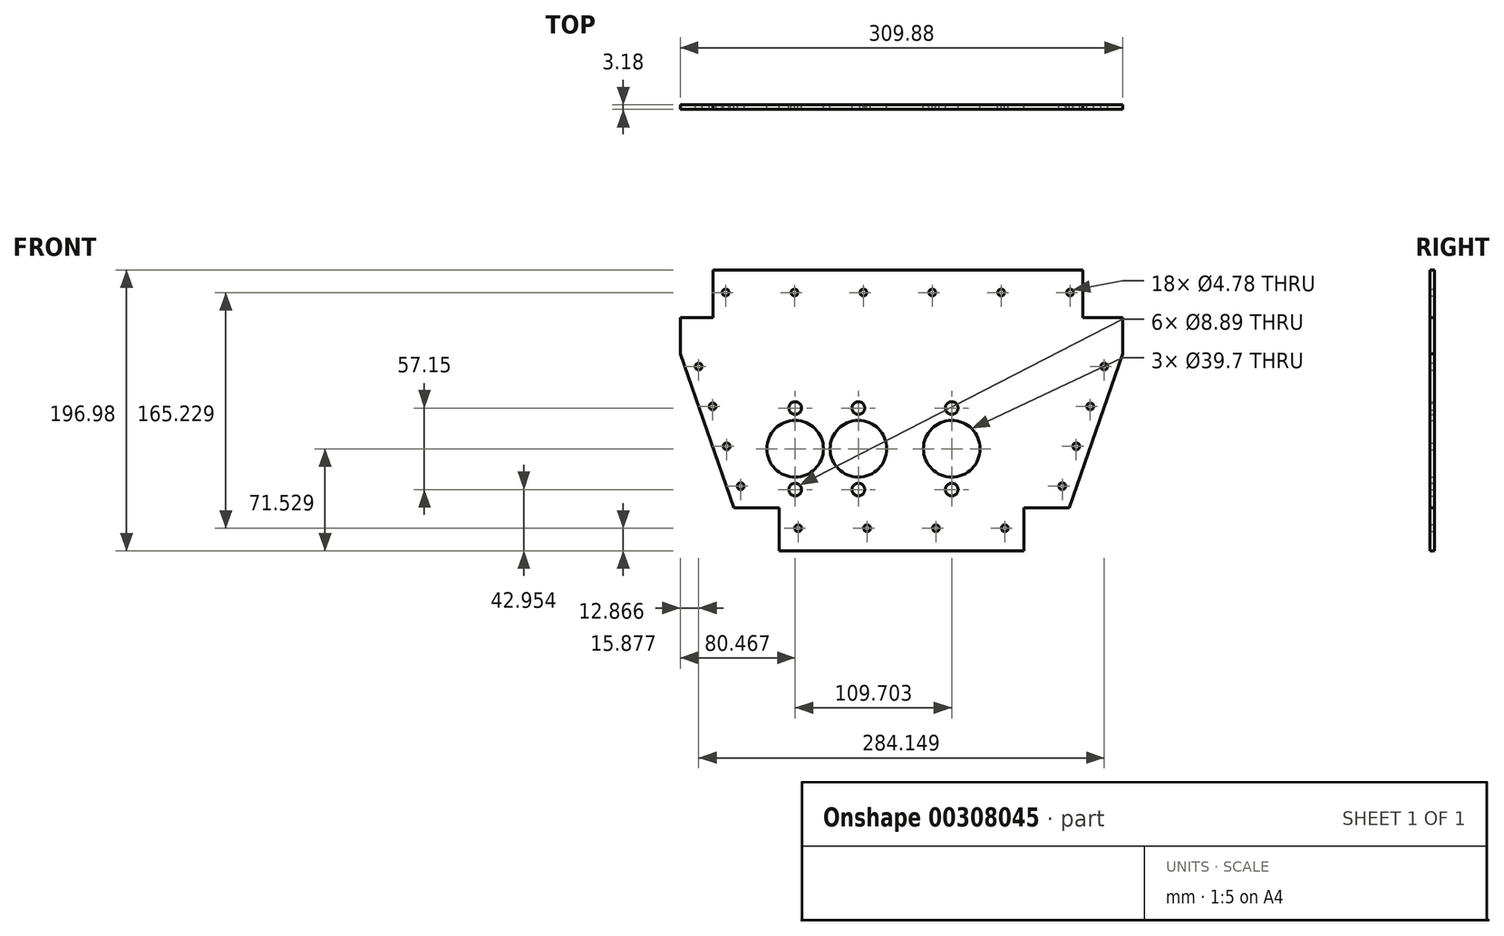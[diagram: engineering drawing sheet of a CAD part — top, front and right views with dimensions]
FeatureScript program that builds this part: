
annotation { "Feature Type Name" : "Feature", "Feature Type Description" : "" }
export const myFeature = defineFeature(function(context is Context, id is Id, definition is map)
    precondition{}
    {
        {
            var Q0;
            Q0=qCreatedBy(makeId("Front.planeOp"),FACE);
            var sketch = newSketch(context, id + "F0", { "sketchPlane" : qUnion([Q0])});
            skLineSegment(sketch, "E0.bottom", {"start": v(85.73, -97.64) * mm, "end": v(-85.73, -97.64) * mm});
            skLineSegment(sketch, "E0.top", {"start": v(127, 99.34) * mm, "end": v(-132.08, 99.34) * mm});
            skPoint(sketch, "E0.middle", {"position": v(0, 0) * mm});
            skLineSegment(sketch, "E1.0", {"start": v(-132.08, 99.34) * mm, "end": v(-132.08, 65.89) * mm});
            skLineSegment(sketch, "E2.trimOffspring", {"start": v(-132.08, 65.89) * mm, "end": v(-154.94, 65.89) * mm});
            skLineSegment(sketch, "E3.MirrorCS", {"start": v(127, 99.34) * mm, "end": v(127, 65.89) * mm});
            skLineSegment(sketch, "E4.MirrorCS", {"start": v(127, 65.89) * mm, "end": v(154.94, 65.89) * mm});
            skLineSegment(sketch, "E5.0", {"start": v(117.48, -67.46) * mm, "end": v(85.72, -67.46) * mm});
            skLineSegment(sketch, "E6", {"start": v(-154.94, 40.49) * mm, "end": v(-117.48, -67.46) * mm});
            skLineSegment(sketch, "E7.trimOffspring", {"start": v(-154.94, 40.49) * mm, "end": v(-154.94, 65.89) * mm});
            skLineSegment(sketch, "E8.MirrorCS", {"start": v(154.94, 40.49) * mm, "end": v(117.48, -67.46) * mm});
            skLineSegment(sketch, "E9.trimOffspring", {"start": v(154.94, 40.49) * mm, "end": v(154.94, 65.89) * mm});
            skLineSegment(sketch, "E10.0", {"start": v(-85.73, -67.46) * mm, "end": v(-85.73, -97.64) * mm});
            skLineSegment(sketch, "E11.trimOffspring", {"start": v(-85.73, -67.46) * mm, "end": v(-117.48, -67.46) * mm});
            skLineSegment(sketch, "E12.0", {"start": v(85.72, -67.46) * mm, "end": v(85.73, -97.64) * mm});
            skCircle(sketch, "E13", {"center": v(-74.47, -26.11) * mm, "radius": 19.85 * mm});
            skCircle(sketch, "E14", {"center": v(-30.18, -26.11) * mm, "radius": 19.85 * mm});
            skCircle(sketch, "E15", {"center": v(35.23, -26.11) * mm, "radius": 19.85 * mm});
            skCircle(sketch, "E16", {"center": v(-74.47, 2.46) * mm, "radius": 4.45 * mm});
            skCircle(sketch, "E17", {"center": v(-30.18, 2.46) * mm, "radius": 4.45 * mm});
            skCircle(sketch, "E18", {"center": v(35.23, 2.46) * mm, "radius": 4.45 * mm});
            skCircle(sketch, "E19", {"center": v(-74.47, -54.69) * mm, "radius": 4.45 * mm});
            skCircle(sketch, "E20", {"center": v(-30.18, -54.69) * mm, "radius": 4.45 * mm});
            skCircle(sketch, "E21", {"center": v(35.23, -54.69) * mm, "radius": 4.45 * mm});
            skCircle(sketch, "E22", {"center": v(-123.2, 83.47) * mm, "radius": 2.39 * mm});
            skCircle(sketch, "E23.1.0.0", {"center": v(-74.93, 83.47) * mm, "radius": 2.39 * mm});
            skCircle(sketch, "E23.2.0.0", {"center": v(-26.67, 83.47) * mm, "radius": 2.39 * mm});
            skCircle(sketch, "E23.3.0.0", {"center": v(21.59, 83.47) * mm, "radius": 2.39 * mm});
            skCircle(sketch, "E23.4.0.0", {"center": v(69.85, 83.47) * mm, "radius": 2.39 * mm});
            skCircle(sketch, "E23.5.0.0", {"center": v(118.1, 83.47) * mm, "radius": 2.39 * mm});
            skCircle(sketch, "E24", {"center": v(112.64, -52.34) * mm, "radius": 2.39 * mm});
            skCircle(sketch, "E25", {"center": v(122.45, -24.37) * mm, "radius": 2.39 * mm});
            skCircle(sketch, "E26", {"center": v(132.26, 3.6) * mm, "radius": 2.39 * mm});
            skCircle(sketch, "E27", {"center": v(142.07, 31.57) * mm, "radius": 2.39 * mm});
            skCircle(sketch, "E28.MirrorC", {"center": v(-112.64, -52.34) * mm, "radius": 2.39 * mm});
            skCircle(sketch, "E29.MirrorC", {"center": v(-132.26, 3.6) * mm, "radius": 2.39 * mm});
            skCircle(sketch, "E30.MirrorC", {"center": v(-142.07, 31.57) * mm, "radius": 2.39 * mm});
            skCircle(sketch, "E31.MirrorC", {"center": v(-122.45, -24.37) * mm, "radius": 2.39 * mm});
            skCircle(sketch, "E32", {"center": v(-72.4, -81.76) * mm, "radius": 2.39 * mm});
            skCircle(sketch, "E33.1.0.0", {"center": v(-24.13, -81.76) * mm, "radius": 2.39 * mm});
            skCircle(sketch, "E33.2.0.0", {"center": v(24.13, -81.76) * mm, "radius": 2.39 * mm});
            skCircle(sketch, "E33.3.0.0", {"center": v(72.4, -81.76) * mm, "radius": 2.39 * mm});
            skSolve(sketch);
        }
        {
            var Q0;
            Q0=makeQuery(id+"F0.imprint","IMPRINT",FACE,{"disambiguationData":[TD([[makeQuery(id+"F0.imprint","IMPRINT",EDGE,{"derivedFrom":sQuery(id+"F0.wireOp",EDGE,"E0.bottom")}),-1.0]])]});
            extrude(context, id + "F1", {"entities" : qUnion([Q0]), "depth" : 3.17 * mm});
        }
    });
